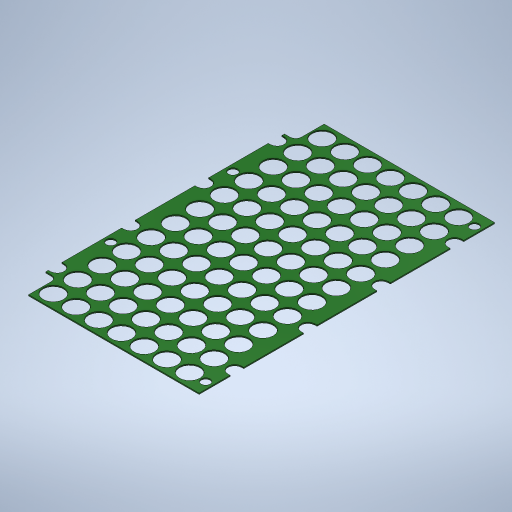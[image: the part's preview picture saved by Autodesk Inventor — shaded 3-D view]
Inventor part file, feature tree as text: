
AUTODESK INVENTOR PART (.ipt)
format: ipt  version: 2024 (Build 280153000, 153)  size: 549,376 bytes
history: native  units: mm
features: extrude x1, sketch x1
ambient origin geometry x8: Origin, YZ Plane, XZ Plane, XY Plane, X Axis, Y Axis, Z Axis, Center Point
bodies: Body1 (feature_tree)
feature tree (2):
  extrude  "Extrusion3"  Depth=1.0mm
  sketch  "Skizze3"  dims[d21=1.0mm d22=0.0mm d49=7.0mm d50=3.0mm d51=10.75mm]
